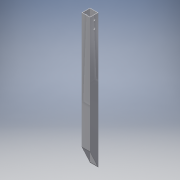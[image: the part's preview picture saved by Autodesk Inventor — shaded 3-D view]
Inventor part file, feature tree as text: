
AUTODESK INVENTOR PART (.ipt)
format: ipt  version: 2016 (Build 200138000, 138)  size: 128,512 bytes
history: native  units: in
note: dims shown in document units (in); Inventor stores cm internally (conversion verified against a paired STEP export)
features: sketch x4, other x3
ambient origin geometry x8: Origin, YZ Plane, XZ Plane, XY Plane, X Axis, Y Axis, Z Axis, Center Point
bodies: Solid1 (feature_tree)
feature tree (7):
  other  "top.ipt"
  other  "Solid1::top.ipt"
  other  "TaggingFeature1"
  sketch  "Sketch1"  dims[d0=0.3937in]
  sketch  "Sketch2"
  sketch  "Sketch3"
  sketch  "Sketch4"
